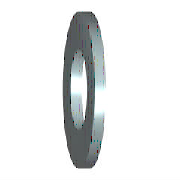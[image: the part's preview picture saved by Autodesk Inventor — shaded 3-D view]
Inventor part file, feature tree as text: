
AUTODESK INVENTOR PART (.ipt)
format: ipt  version: 2015 (Build 190159000, 159)  size: 108,544 bytes
history: native  units: mm (DEFAULTED — no unit token found)
features: extrude x1, other x1, plane x1, sketch x1
ambient origin geometry x7: Origin, YZ Plane, XY Plane, X Axis, Y Axis, Z Axis, Center Point
bodies: Solid1 (feature_tree)
feature tree (4):
  extrude  "Bryła"  Depth=6.4mm
  other  "Work Axis1"
  plane  "Work Plane1"
  sketch  "Szkic"
